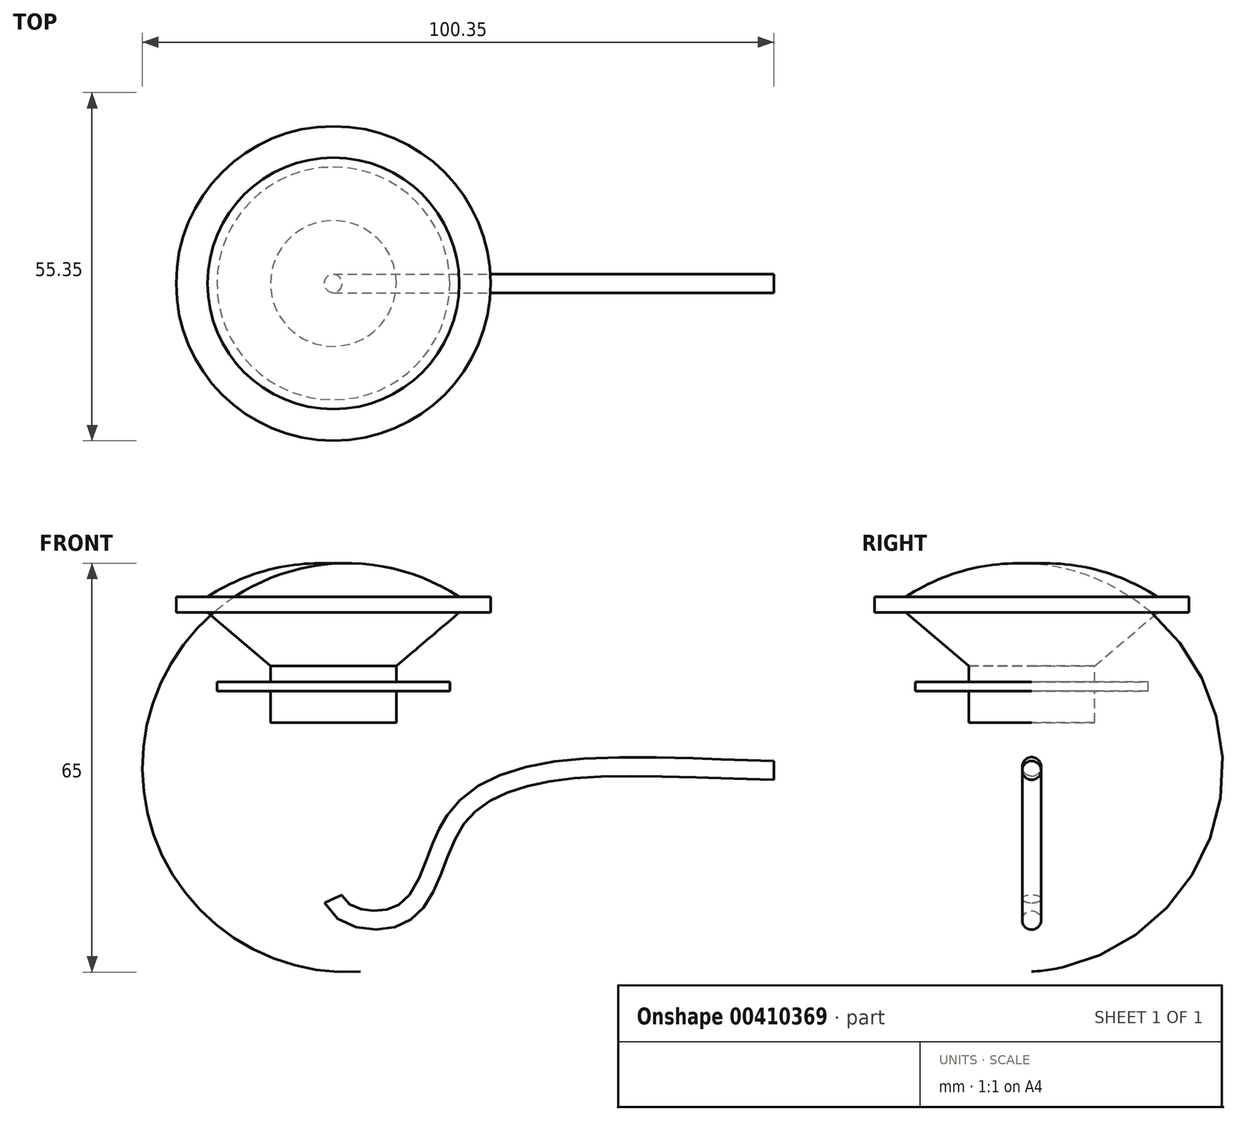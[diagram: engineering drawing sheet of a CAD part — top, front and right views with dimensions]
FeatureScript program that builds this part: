
annotation { "Feature Type Name" : "Feature", "Feature Type Description" : "" }
export const myFeature = defineFeature(function(context is Context, id is Id, definition is map)
    precondition{}
    {
        {
            var Q0;
            Q0=qCreatedBy(makeId("Front.planeOp"),FACE);
            var sketch = newSketch(context, id + "F0", { "sketchPlane" : qUnion([Q0])});
            skLineSegment(sketch, "E0", {"start": v(0, 65.95) * mm, "end": v(0, -66.2) * mm, "construction": true});
            skArc(sketch, "E1", {"start": v(40, 40.66) * mm, "mid": v(20.86, 49.2) * mm, "end": v(0, 51.2) * mm});
            skLineSegment(sketch, "E2", {"start": v(40, 40.66) * mm, "end": v(50, 40.66) * mm});
            skLineSegment(sketch, "E3", {"start": v(50, 40.66) * mm, "end": v(50, 35.66) * mm});
            skLineSegment(sketch, "E4", {"start": v(50, 35.66) * mm, "end": v(40, 35.66) * mm});
            skLineSegment(sketch, "E5", {"start": v(40, 35.66) * mm, "end": v(20, 18.66) * mm});
            skLineSegment(sketch, "E6", {"start": v(20, 18.66) * mm, "end": v(20, 13.66) * mm});
            skLineSegment(sketch, "E7", {"start": v(20, 13.66) * mm, "end": v(37, 13.66) * mm});
            skLineSegment(sketch, "E8", {"start": v(37, 13.66) * mm, "end": v(37, 10.66) * mm});
            skLineSegment(sketch, "E9", {"start": v(37, 10.66) * mm, "end": v(20, 10.66) * mm});
            skLineSegment(sketch, "E10", {"start": v(20, 10.66) * mm, "end": v(20, 0.66) * mm});
            skLineSegment(sketch, "E11", {"start": v(20, 0.66) * mm, "end": v(0, 0.66) * mm});
            skLineSegment(sketch, "E12", {"start": v(0, 0.66) * mm, "end": v(0, 51.2) * mm});
            skSolve(sketch);
        }
        {
            var Q0;
            Q0=makeQuery(id+"F0.imprint","IMPRINT",FACE,{"disambiguationData":[TD([[makeQuery(id+"F0.imprint","IMPRINT",EDGE,{"derivedFrom":sQuery(id+"F0.wireOp",EDGE,"E1")}),1.0]])]});
            var Q1;
            Q1=sQuery(id+"F0.wireOp",EDGE,"E0");
            revolve(context, id + "F1", {"entities" : qUnion([Q0]), "axis" : qUnion([Q1]), "revolveType" : RevolveType.FULL});
        }
        {
            var Q0;
            Q0=makeQuery(id+"F1.opRevolve","SWEPT_BODY",BODY,{"disambiguationData":[OSD([sQuery(id+"F0.wireOp",EDGE,"E1"),sQuery(id+"F0.wireOp",EDGE,"E2"),sQuery(id+"F0.wireOp",EDGE,"E3"),sQuery(id+"F0.wireOp",EDGE,"E4"),sQuery(id+"F0.wireOp",EDGE,"E5"),sQuery(id+"F0.wireOp",EDGE,"E6"),sQuery(id+"F0.wireOp",EDGE,"E7"),sQuery(id+"F0.wireOp",EDGE,"E8"),sQuery(id+"F0.wireOp",EDGE,"E9"),sQuery(id+"F0.wireOp",EDGE,"E10"),sQuery(id+"F0.wireOp",EDGE,"E11"),sQuery(id+"F0.wireOp",EDGE,"E12")])]});
            var Q1;
            Q1=qCreatedBy(makeId("Origin.pointOp"),VERTEX);
            transform(context, id + "F2", {"entities" : qUnion([Q0]), "transformType" : TransformType.SCALE_UNIFORMLY, "scale" : .5, "scalePoint" : qUnion([Q1]), "makeCopy" : false});
        }
        {
            var Q0;
            Q0=qCreatedBy(makeId("Front.planeOp"),FACE);
            var sketch = newSketch(context, id + "F3", { "sketchPlane" : qUnion([Q0])});
            skLineSegment(sketch, "E13", {"start": v(0, 39.37) * mm, "end": v(0, -38.32) * mm, "construction": true});
            skFitSpline(sketch, "E14", {"points": [v(0, -27.67) * mm, v(8.16, -30.94) * mm, v(14.26, -26.37) * mm, v(19.7, -14.6) * mm, v(33.2, -7.64) * mm, v(70, -7.2) * mm], "startDerivative": vector(22.09, -53.34) * mm, "endDerivative": vector(152.4, -4.38) * mm});
            skSolve(sketch);
        }
        {
            var Q0;
            Q0=qCreatedBy(makeId("Right.planeOp"),FACE);
            cPlane(context, id + "F4", {"entities" : qUnion([Q0]), "cplaneType" : CPlaneType.OFFSET, "offset" : 70 * mm, "width" : 150 * mm, "height" : 150 * mm});
        }
        {
            var Q0;
            Q0=qCreatedBy(id+"F4.planeOp",FACE);
            var sketch = newSketch(context, id + "F5", { "sketchPlane" : qUnion([Q0])});
            skCircle(sketch, "E15", {"center": v(0, -7.25) * mm, "radius": 1.5 * mm});
            skSolve(sketch);
        }
        {
            var Q0;
            Q0=makeQuery(id+"F5.imprint","IMPRINT",FACE,{"disambiguationData":[TD([[makeQuery(id+"F5.imprint","IMPRINT",EDGE,{"derivedFrom":sQuery(id+"F5.wireOp",EDGE,"E15")}),1.0]])]});
            var Q1;
            Q1=sQuery(id+"F3.wireOp",EDGE,"E14");
            sweep(context, id + "F6", {"profiles" : qUnion([Q0]), "path" : qUnion([Q1])});
        }
    });
